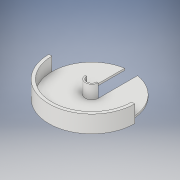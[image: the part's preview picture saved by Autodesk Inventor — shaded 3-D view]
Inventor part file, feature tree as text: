
AUTODESK INVENTOR PART (.ipt)
format: ipt  version: 2017 (Build 210142000, 142)  size: 161,792 bytes
history: native  units: in
note: dims shown in document units (in); Inventor stores cm internally (conversion verified against a paired STEP export)
features: sketch x9, extrude x8, projected_geometry x1
ambient origin geometry x8: Origin, YZ Plane, XZ Plane, XY Plane, X Axis, Y Axis, Z Axis, Center Point
bodies: Solid1 (feature_tree)
feature tree (18):
  extrude  "Extrusion1"  Depth=1.1024in TaperAngle=0.0deg
  extrude  "Extrusion2"  Depth=11.0236in TaperAngle=0.0deg
  extrude  "Extrusion3"  Depth=0.8268in
  extrude  "Extrusion4"  Depth=0.8661in TaperAngle=0.0deg
  extrude  "Extrusion5"  Depth=0.1181in TaperAngle=0.0deg
  extrude  "Extrusion6"  Depth=0.1181in TaperAngle=0.0deg
  sketch  "Sketch7"
  extrude  "Extrusion7"  [1 undecoded]
  extrude  "Extrusion8"  [1 undecoded]
  sketch  "Sketch1"  dims[d0=5.5118in d1=1.1024in d2=0.0in]
  sketch  "Sketch2"  dims[d3=0.6496in d4=11.0236in d5=0.0in]
  sketch  "Sketch3"  dims[d6=5.1181in d7=0.8268in]
  sketch  "Sketch4"  dims[d8=0.8661in d9=0.0in d10=8.6614in d11=0.0in]
  sketch  "Sketch5"  dims[d12=0.1181in d13=0.0in d14=0.1181in d15=0.0in]
  sketch  "Sketch6"  dims[d16=0.1181in d17=0.0in d18=1.1811in d19=0.0in]
  projected_geometry  "Projected Loop1"
  sketch  "Sketch8"
  sketch  "Sketch9"
note: 2 required parameter values undecoded (feature->parameter linkage not recoverable at this tier; creation-order binding heuristic only, values carry confidence <= 0.55)
